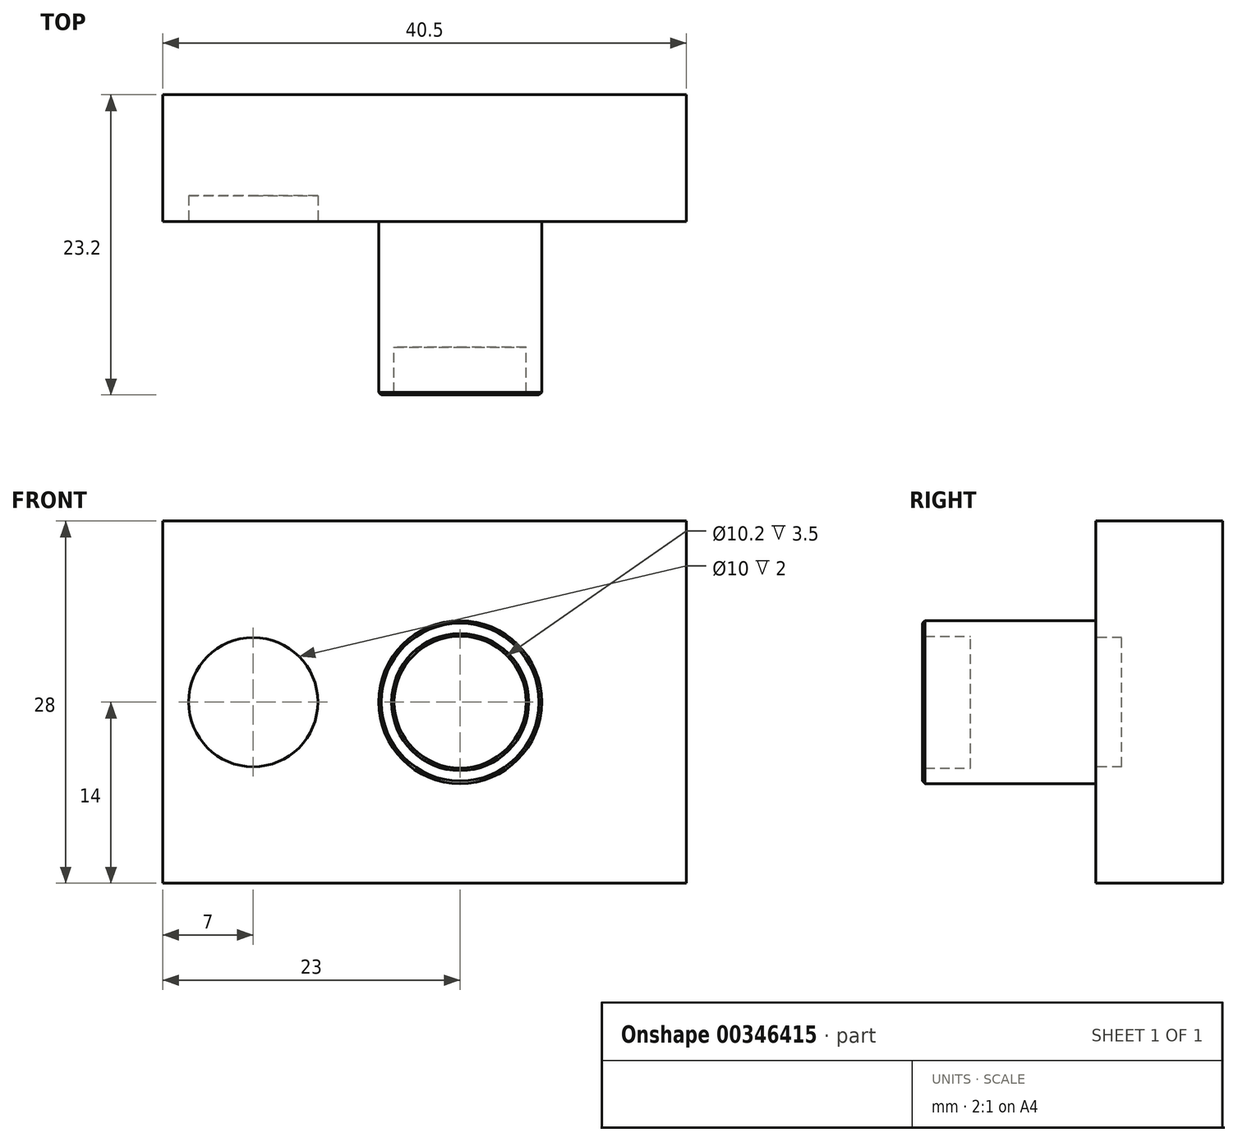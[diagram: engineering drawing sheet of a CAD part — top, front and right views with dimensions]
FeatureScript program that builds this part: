
annotation { "Feature Type Name" : "Feature", "Feature Type Description" : "" }
export const myFeature = defineFeature(function(context is Context, id is Id, definition is map)
    precondition{}
    {
        {
            var Q0;
            Q0=qCreatedBy(makeId("Front.planeOp"),FACE);
            var sketch = newSketch(context, id + "F0", { "sketchPlane" : qUnion([Q0])});
            skLineSegment(sketch, "E0.bottom", {"start": v(0, 0) * mm, "end": v(40.5, 0) * mm});
            skLineSegment(sketch, "E0.top", {"start": v(0, -28) * mm, "end": v(40.5, -28) * mm});
            skLineSegment(sketch, "E0.left", {"start": v(0, 0) * mm, "end": v(0, -28) * mm});
            skLineSegment(sketch, "E0.right", {"start": v(40.5, 0) * mm, "end": v(40.5, -28) * mm});
            skSolve(sketch);
        }
        {
            var Q0;
            Q0 = qSketchRegion(id + "F0", true);
            extrude(context, id + "F1", {"entities" : qUnion([Q0]), "depth" : 9.8 * mm});
        }
        {
            var Q0;
            Q0=makeQuery(id+"F1.opExtrude","CAP_FACE",FACE,{"disambiguationData":[OSD([sQuery(id+"F0.wireOp",EDGE,"E0.bottom"),sQuery(id+"F0.wireOp",EDGE,"E0.top"),sQuery(id+"F0.wireOp",EDGE,"E0.left"),sQuery(id+"F0.wireOp",EDGE,"E0.right")])],"isStart":false});
            var sketch = newSketch(context, id + "F2", { "sketchPlane" : qUnion([Q0])});
            skCircle(sketch, "E1", {"center": v(23, -14) * mm, "radius": 6.3 * mm});
            skCircle(sketch, "E2", {"center": v(23, -14) * mm, "radius": 5.1 * mm});
            skLineSegment(sketch, "E3", {"start": v(23, -14) * mm, "end": v(23, 0) * mm, "construction": true});
            skLineSegment(sketch, "E4", {"start": v(23, -14) * mm, "end": v(23, -28) * mm, "construction": true});
            skLineSegment(sketch, "E5", {"start": v(23, -14) * mm, "end": v(40.5, -14) * mm, "construction": true});
            skLineSegment(sketch, "E6", {"start": v(29.3, -14) * mm, "end": v(40.5, -14) * mm, "construction": true});
            skSolve(sketch);
        }
        {
            var Q0;
            Q0=makeQuery(id+"F2.imprint","IMPRINT",FACE,{"disambiguationData":[TD([[makeQuery(id+"F2.imprint","IMPRINT",EDGE,{"derivedFrom":sQuery(id+"F2.wireOp",EDGE,"E1")}),1.0]])]});
            extrude(context, id + "F3", {"entities" : qUnion([Q0]), "operationType" : NewBodyOperationType.ADD, "depth" : 13.4 * mm});
        }
        {
            var Q0;
            Q0=makeQuery(id+"F3.boolean.opBoolean","SPLIT",FACE,{"disambiguationData":[TD([makeQuery(id+"F3.opExtrude","SWEPT_FACE",FACE,{"disambiguationData":[OSD([sQuery(id+"F2.wireOp",EDGE,"E2")])]})])],"derivedFrom":makeQuery(id+"F1.opExtrude","CAP_FACE",FACE,{"disambiguationData":[OSD([sQuery(id+"F0.wireOp",EDGE,"E0.bottom"),sQuery(id+"F0.wireOp",EDGE,"E0.top"),sQuery(id+"F0.wireOp",EDGE,"E0.left"),sQuery(id+"F0.wireOp",EDGE,"E0.right")])],"isStart":false})});
            extrude(context, id + "F4", {"entities" : qUnion([Q0]), "operationType" : NewBodyOperationType.ADD, "depth" : 9.7 * mm});
        }
        {
            var Q0;
            {var subQ0=sQuery(id+"F0.wireOp",EDGE,"E0.left");var subQ1=sQuery(id+"F0.wireOp",EDGE,"E0.top");var subQ2=sQuery(id+"F0.wireOp",EDGE,"E0.right");var subQ3=sQuery(id+"F0.wireOp",EDGE,"E0.bottom");Q0=makeQuery(id+"F3.boolean.opBoolean","SPLIT",FACE,{"disambiguationData":[TD([makeQuery(id+"F1.opExtrude","SWEPT_FACE",FACE,{"disambiguationData":[OSD([subQ3])]})])],"derivedFrom":makeQuery(id+"F1.opExtrude","CAP_FACE",FACE,{"disambiguationData":[OSD([subQ3,subQ1,subQ0,subQ2])],"isStart":false})});}
            var sketch = newSketch(context, id + "F5", { "sketchPlane" : qUnion([Q0])});
            skCircle(sketch, "E7", {"center": v(7, -14) * mm, "radius": 5 * mm});
            skLineSegment(sketch, "E8", {"start": v(7, -14) * mm, "end": v(7, 0) * mm, "construction": true});
            skLineSegment(sketch, "E9", {"start": v(7, -14) * mm, "end": v(7, -28) * mm, "construction": true});
            skLineSegment(sketch, "E10", {"start": v(7, -14) * mm, "end": v(0, -14) * mm, "construction": true});
            skSolve(sketch);
        }
        {
            var Q0;
            Q0=makeQuery(id+"F5.imprint","IMPRINT",FACE,{"disambiguationData":[TD([[makeQuery(id+"F5.imprint","IMPRINT",EDGE,{"derivedFrom":sQuery(id+"F5.wireOp",EDGE,"E7")}),1.0]])]});
            extrude(context, id + "F6", {"entities" : qUnion([Q0]), "operationType" : NewBodyOperationType.REMOVE, "oppositeDirection" : true, "depth" : 2 * mm});
        }
        {
            var Q0;
            Q0=makeQuery(id+"F3.opExtrude","CAP_EDGE",EDGE,{"disambiguationData":[OSD([sQuery(id+"F2.wireOp",EDGE,"E2")])],"isStart":false});
            var Q1;
            Q1=makeQuery(id+"F3.opExtrude","CAP_EDGE",EDGE,{"disambiguationData":[OSD([sQuery(id+"F2.wireOp",EDGE,"E1")])],"isStart":false});
            chamfer(context, id + "F7", {"entities" : qUnion([Q0, Q1]), "width" : 0.2 * mm, "tangentPropagation" : true});
        }
    });
